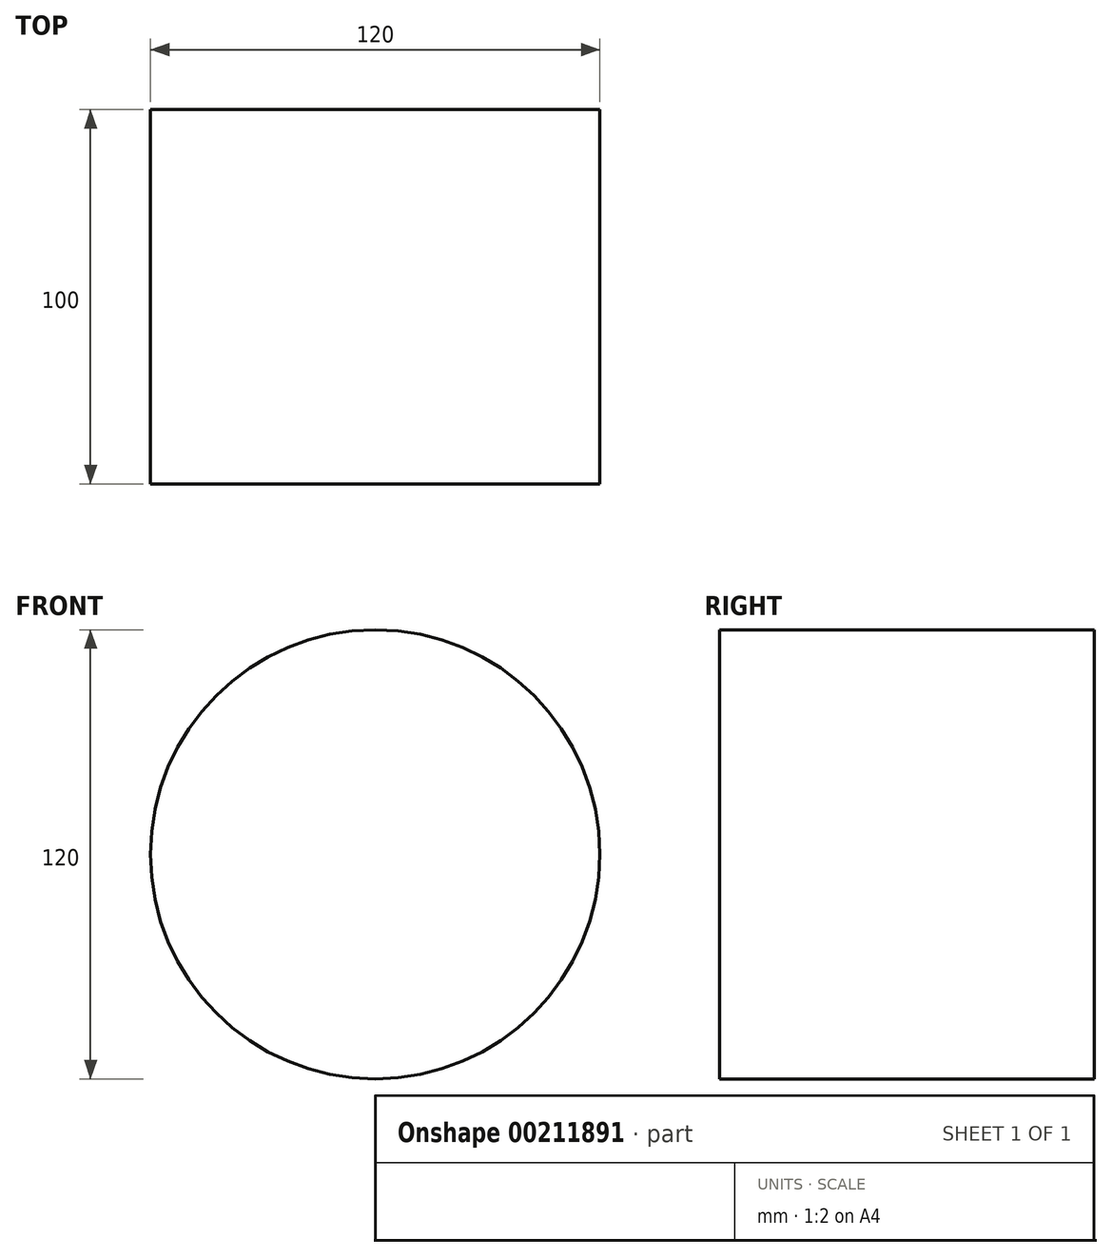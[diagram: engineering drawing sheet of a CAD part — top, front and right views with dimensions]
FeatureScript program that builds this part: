
annotation { "Feature Type Name" : "Feature", "Feature Type Description" : "" }
export const myFeature = defineFeature(function(context is Context, id is Id, definition is map)
    precondition{}
    {
        {
            var Q0;
            Q0=qCreatedBy(makeId("Front.planeOp"),FACE);
            var sketch = newSketch(context, id + "F0", { "sketchPlane" : qUnion([Q0])});
            skCircle(sketch, "E0", {"center": v(6.66, -18.83) * mm, "radius": 60 * mm});
            skSolve(sketch);
        }
        {
            var Q0;
            Q0=makeQuery(id+"F0.imprint","IMPRINT",FACE,{"disambiguationData":[TD([[makeQuery(id+"F0.imprint","IMPRINT",EDGE,{"derivedFrom":sQuery(id+"F0.wireOp",EDGE,"E0")}),1.0]])]});
            extrude(context, id + "F1", {"entities" : qUnion([Q0]), "depth" : 100 * mm});
        }
    });
